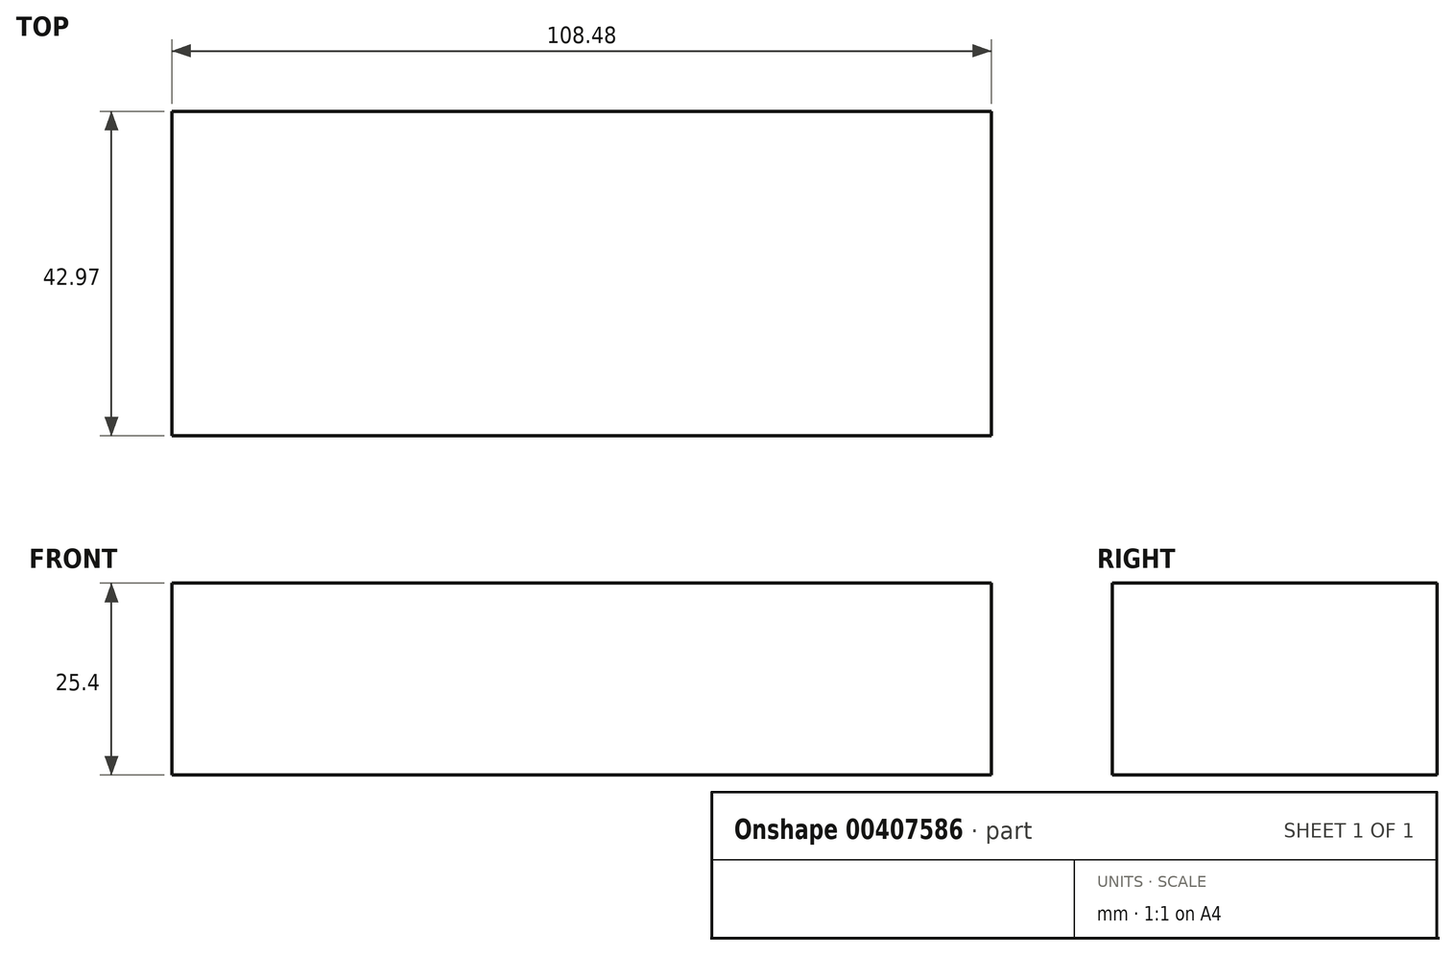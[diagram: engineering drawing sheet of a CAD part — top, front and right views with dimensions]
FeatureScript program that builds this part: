
annotation { "Feature Type Name" : "Feature", "Feature Type Description" : "" }
export const myFeature = defineFeature(function(context is Context, id is Id, definition is map)
    precondition{}
    {
        {
            var Q0;
            Q0=qCreatedBy(makeId("Top.planeOp"),FACE);
            var sketch = newSketch(context, id + "F0", { "sketchPlane" : qUnion([Q0])});
            skLineSegment(sketch, "E0", {"start": v(-64.67, 21.78) * mm, "end": v(46.42, 21.78) * mm});
            skLineSegment(sketch, "E1", {"start": v(46.42, 21.78) * mm, "end": v(46.42, -21.2) * mm});
            skLineSegment(sketch, "E2", {"start": v(46.42, -21.2) * mm, "end": v(-62.06, -21.2) * mm});
            skLineSegment(sketch, "E3", {"start": v(-62.06, -21.2) * mm, "end": v(-62.06, 21.78) * mm});
            skSolve(sketch);
        }
        {
            var Q0;
            Q0 = qSketchRegion(id + "F0", true);
            var Q1;
            {var subQ0=sQuery(id+"F0.wireOp",EDGE,"E1");Q1=makeQuery(id+"F0.imprint","IMPRINT",FACE,{"disambiguationData":[TD([[makeQuery(id+"F0.imprint","IMPRINT",EDGE,{"derivedFrom":subQ0}),-1.0]])]});}
            extrude(context, id + "F1", {"entities" : qUnion([Q0, Q1]), "depth" : 25.4 * mm});
        }
    });
